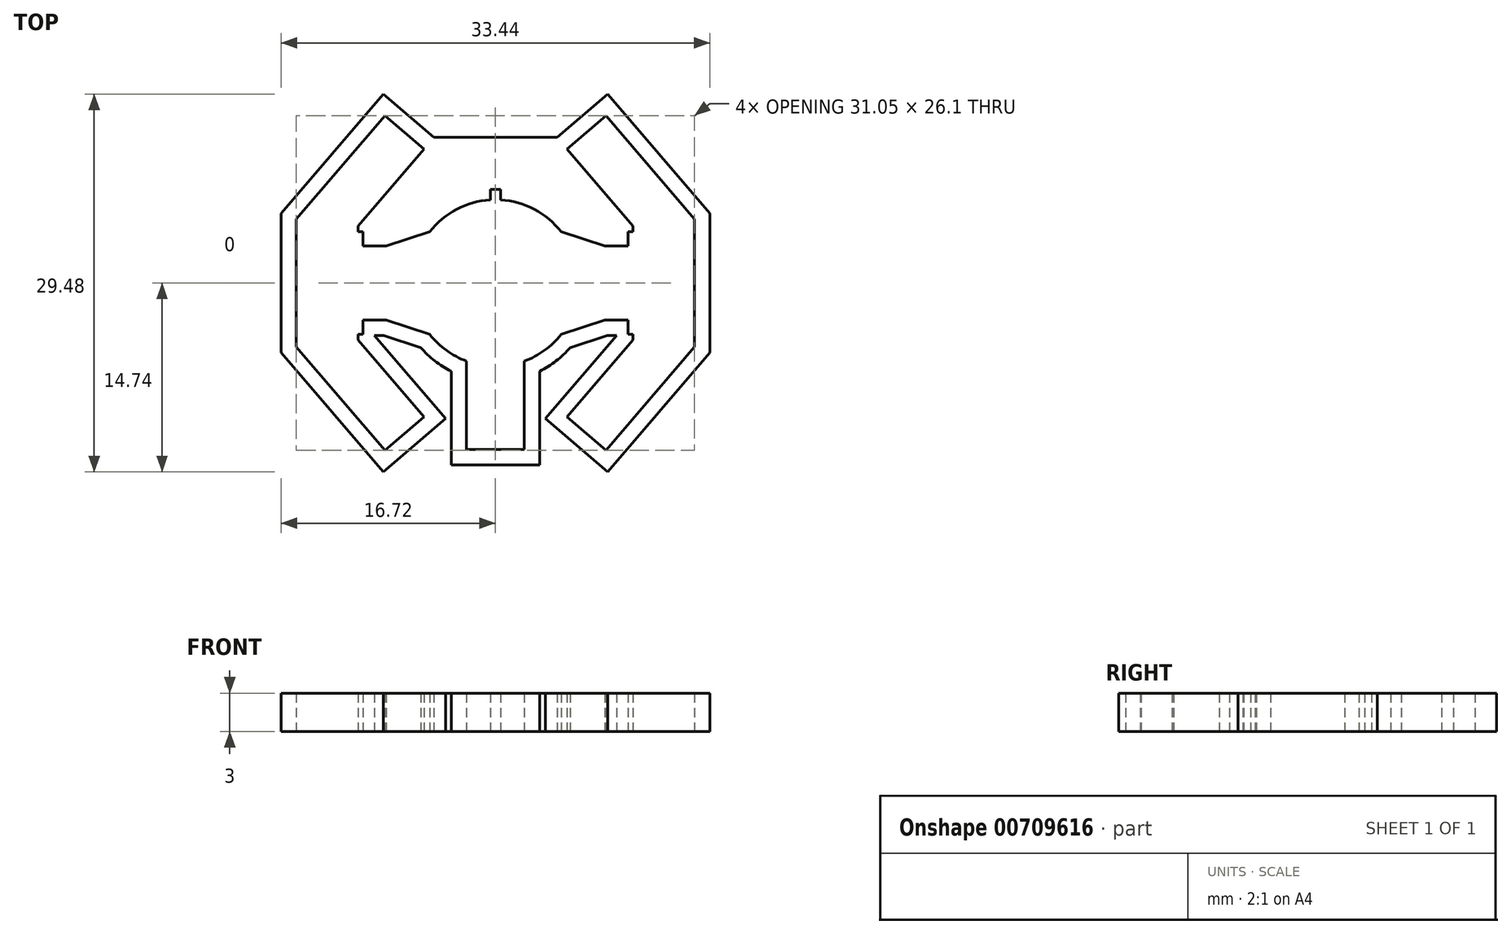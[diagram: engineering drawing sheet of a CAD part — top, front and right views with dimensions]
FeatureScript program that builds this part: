
annotation { "Feature Type Name" : "Feature", "Feature Type Description" : "" }
export const myFeature = defineFeature(function(context is Context, id is Id, definition is map)
    precondition{}
    {
        {
            var Q0;
            Q0=qCreatedBy(makeId("Top.planeOp"),FACE);
            var sketch = newSketch(context, id + "F0", { "sketchPlane" : qUnion([Q0])});
            skArc(sketch, "E0.0", {"start": v(-5.12, -4) * mm, "mid": v(-3.83, -5.25) * mm, "end": v(-2.25, -6.1) * mm});
            skLineSegment(sketch, "E0.1", {"start": v(8.52, 2.9) * mm, "end": v(10.32, 2.9) * mm});
            skLineSegment(sketch, "E0.2", {"start": v(5.12, 4) * mm, "end": v(8.52, 2.9) * mm});
            skArc(sketch, "E0.8", {"start": v(5.12, 4) * mm, "mid": v(3.03, 5.75) * mm, "end": v(0.4, 6.49) * mm});
            skPoint(sketch, "E0.9", {"position": v(0, 0) * mm});
            skLineSegment(sketch, "E0.10", {"start": v(10.72, 4) * mm, "end": v(10.32, 4) * mm});
            skLineSegment(sketch, "E0.11", {"start": v(10.32, 4) * mm, "end": v(10.32, 2.9) * mm});
            skLineSegment(sketch, "E0.12", {"start": v(-2.25, -13) * mm, "end": v(2.25, -13) * mm});
            skLineSegment(sketch, "E0.13", {"start": v(-2.25, -13) * mm, "end": v(-2.25, -6.1) * mm});
            skLineSegment(sketch, "E0.14", {"start": v(2.25, -13) * mm, "end": v(2.25, -6.1) * mm});
            skArc(sketch, "E0.15", {"start": v(-2.25, -6.1) * mm, "mid": v(-3.83, -5.25) * mm, "end": v(-5.12, -4) * mm});
            skLineSegment(sketch, "E0.16", {"start": v(0, 7.3) * mm, "end": v(0.4, 7.3) * mm});
            skLineSegment(sketch, "E0.17", {"start": v(0.4, 7.3) * mm, "end": v(0.4, 6.49) * mm});
            skLineSegment(sketch, "E0.18", {"start": v(0, 7.3) * mm, "end": v(-0.4, 7.3) * mm});
            skLineSegment(sketch, "E0.19", {"start": v(-0.4, 7.3) * mm, "end": v(-0.4, 6.49) * mm});
            skArc(sketch, "E0.20", {"start": v(0.4, 6.49) * mm, "mid": v(3.03, 5.75) * mm, "end": v(5.12, 4) * mm});
            skLineSegment(sketch, "E0.22", {"start": v(10.72, 4.44) * mm, "end": v(10.72, 4) * mm});
            skLineSegment(sketch, "E0.44", {"start": v(15.52, 4.99) * mm, "end": v(15.52, 0) * mm});
            skLineSegment(sketch, "E0.48", {"start": v(0, 23) * mm, "end": v(0, -39.67) * mm, "construction": true});
            skLineSegment(sketch, "E0.49", {"start": v(-35.38, 0) * mm, "end": v(37.32, 0) * mm, "construction": true});
            skArc(sketch, "E0.82", {"start": v(5.12, -4) * mm, "mid": v(3.83, -5.25) * mm, "end": v(2.25, -6.1) * mm});
            skLineSegment(sketch, "E1", {"start": v(8.62, 13.05) * mm, "end": v(5.58, 10.45) * mm});
            skLineSegment(sketch, "E2", {"start": v(5.58, 10.45) * mm, "end": v(10.72, 4.44) * mm});
            skLineSegment(sketch, "E3", {"start": v(8.62, 13.05) * mm, "end": v(15.52, 4.99) * mm});
            skLineSegment(sketch, "E4.MirrorCS", {"start": v(10.72, -4) * mm, "end": v(10.32, -4) * mm});
            skLineSegment(sketch, "E5.MirrorCS", {"start": v(10.32, -4) * mm, "end": v(10.32, -2.9) * mm});
            skLineSegment(sketch, "E6.MirrorCS", {"start": v(10.72, -4.44) * mm, "end": v(10.72, -4) * mm});
            skLineSegment(sketch, "E7.MirrorCS", {"start": v(15.52, -4.99) * mm, "end": v(15.52, 0) * mm});
            skLineSegment(sketch, "E8.MirrorCS", {"start": v(5.58, -10.45) * mm, "end": v(10.72, -4.44) * mm});
            skLineSegment(sketch, "E9.MirrorCS", {"start": v(8.62, -13.05) * mm, "end": v(15.52, -4.99) * mm});
            skLineSegment(sketch, "E10.MirrorCS", {"start": v(8.62, -13.05) * mm, "end": v(5.58, -10.45) * mm});
            skLineSegment(sketch, "E11.MirrorCS", {"start": v(5.12, -4) * mm, "end": v(8.52, -2.9) * mm});
            skLineSegment(sketch, "E12.MirrorCS", {"start": v(8.52, -2.9) * mm, "end": v(10.32, -2.9) * mm});
            skLineSegment(sketch, "E13.MirrorCS", {"start": v(-10.72, -4) * mm, "end": v(-10.32, -4) * mm});
            skLineSegment(sketch, "E14.MirrorCS", {"start": v(-10.32, 4) * mm, "end": v(-10.32, 2.9) * mm});
            skLineSegment(sketch, "E15.MirrorCS", {"start": v(-10.72, 4) * mm, "end": v(-10.32, 4) * mm});
            skLineSegment(sketch, "E16.MirrorCS", {"start": v(-10.72, -4.44) * mm, "end": v(-10.72, -4) * mm});
            skLineSegment(sketch, "E17.MirrorCS", {"start": v(-10.72, 4.44) * mm, "end": v(-10.72, 4) * mm});
            skLineSegment(sketch, "E18.MirrorCS", {"start": v(-10.32, -4) * mm, "end": v(-10.32, -2.9) * mm});
            skLineSegment(sketch, "E19.MirrorCS", {"start": v(-5.12, 4) * mm, "end": v(-8.52, 2.9) * mm});
            skLineSegment(sketch, "E20.MirrorCS", {"start": v(-8.62, 13.05) * mm, "end": v(-15.52, 4.99) * mm});
            skLineSegment(sketch, "E21.MirrorCS", {"start": v(-8.52, 2.9) * mm, "end": v(-10.32, 2.9) * mm});
            skLineSegment(sketch, "E22.MirrorCS", {"start": v(-8.62, 13.05) * mm, "end": v(-5.58, 10.45) * mm});
            skLineSegment(sketch, "E23.MirrorCS", {"start": v(-5.58, 10.45) * mm, "end": v(-10.72, 4.44) * mm});
            skLineSegment(sketch, "E24.MirrorCS", {"start": v(-5.12, -4) * mm, "end": v(-8.52, -2.9) * mm});
            skLineSegment(sketch, "E25.MirrorCS", {"start": v(-8.62, -13.05) * mm, "end": v(-15.52, -4.99) * mm});
            skLineSegment(sketch, "E26.MirrorCS", {"start": v(-5.58, -10.45) * mm, "end": v(-10.72, -4.44) * mm});
            skLineSegment(sketch, "E27.MirrorCS", {"start": v(-8.62, -13.05) * mm, "end": v(-5.58, -10.45) * mm});
            skLineSegment(sketch, "E28.MirrorCS", {"start": v(-8.52, -2.9) * mm, "end": v(-10.32, -2.9) * mm});
            skLineSegment(sketch, "E29.MirrorCS", {"start": v(-15.52, -4.99) * mm, "end": v(-15.52, 0) * mm});
            skLineSegment(sketch, "E30.MirrorCS", {"start": v(-15.52, 4.99) * mm, "end": v(-15.52, 0) * mm});
            skArc(sketch, "E31.MirrorCS", {"start": v(-0.4, 6.49) * mm, "mid": v(-3.03, 5.75) * mm, "end": v(-5.12, 4) * mm});
            skLineSegment(sketch, "E32.0", {"start": v(8.75, 14.74) * mm, "end": v(4.8, 11.36) * mm});
            skLineSegment(sketch, "E32.1", {"start": v(8.75, 14.74) * mm, "end": v(16.72, 5.43) * mm});
            skLineSegment(sketch, "E32.3", {"start": v(8.75, -14.74) * mm, "end": v(16.72, -5.43) * mm});
            skLineSegment(sketch, "E32.4", {"start": v(16.72, -5.43) * mm, "end": v(16.72, 0) * mm});
            skLineSegment(sketch, "E32.5", {"start": v(16.72, 5.43) * mm, "end": v(16.72, 0) * mm});
            skLineSegment(sketch, "E33.0", {"start": v(-8.75, 14.74) * mm, "end": v(-4.8, 11.36) * mm});
            skLineSegment(sketch, "E33.1", {"start": v(-8.75, 14.74) * mm, "end": v(-16.72, 5.43) * mm});
            skLineSegment(sketch, "E33.3", {"start": v(-8.75, -14.74) * mm, "end": v(-16.72, -5.43) * mm});
            skLineSegment(sketch, "E33.4", {"start": v(-16.72, -5.43) * mm, "end": v(-16.72, 0) * mm});
            skLineSegment(sketch, "E33.5", {"start": v(-16.72, 5.43) * mm, "end": v(-16.72, 0) * mm});
            skLineSegment(sketch, "E34", {"start": v(-4.8, 11.36) * mm, "end": v(4.8, 11.36) * mm});
            skLineSegment(sketch, "E35.0", {"start": v(3.45, -14.2) * mm, "end": v(3.45, -6.88) * mm});
            skLineSegment(sketch, "E35.1", {"start": v(-3.45, -14.2) * mm, "end": v(3.45, -14.2) * mm});
            skLineSegment(sketch, "E35.2", {"start": v(-3.45, -14.2) * mm, "end": v(-3.45, -6.88) * mm});
            skArc(sketch, "E36.0", {"start": v(5.83, -5.03) * mm, "mid": v(4.73, -6.08) * mm, "end": v(3.45, -6.88) * mm});
            skLineSegment(sketch, "E36.1", {"start": v(5.83, -5.03) * mm, "end": v(8.71, -4.1) * mm});
            skLineSegment(sketch, "E36.2", {"start": v(8.71, -4.1) * mm, "end": v(9.44, -4.1) * mm});
            skArc(sketch, "E37.0", {"start": v(-5.83, -5.03) * mm, "mid": v(-4.73, -6.08) * mm, "end": v(-3.45, -6.88) * mm});
            skLineSegment(sketch, "E37.1", {"start": v(-5.83, -5.03) * mm, "end": v(-8.71, -4.1) * mm});
            skLineSegment(sketch, "E37.2", {"start": v(-8.71, -4.1) * mm, "end": v(-9.44, -4.1) * mm});
            skLineSegment(sketch, "E38.0", {"start": v(-3.9, -10.58) * mm, "end": v(-9.44, -4.1) * mm});
            skLineSegment(sketch, "E39.0", {"start": v(3.9, -10.58) * mm, "end": v(9.44, -4.1) * mm});
            skLineSegment(sketch, "E40", {"start": v(-3.9, -10.58) * mm, "end": v(-8.75, -14.74) * mm});
            skLineSegment(sketch, "E41", {"start": v(3.9, -10.58) * mm, "end": v(8.75, -14.74) * mm});
            skSolve(sketch);
        }
        {
            var Q0;
            Q0 = qSketchRegion(id + "F0", true);
            extrude(context, id + "F1", {"entities" : qUnion([Q0]), "depth" : 3 * mm, "offsetDistance" : 25 * mm});
        }
    });
